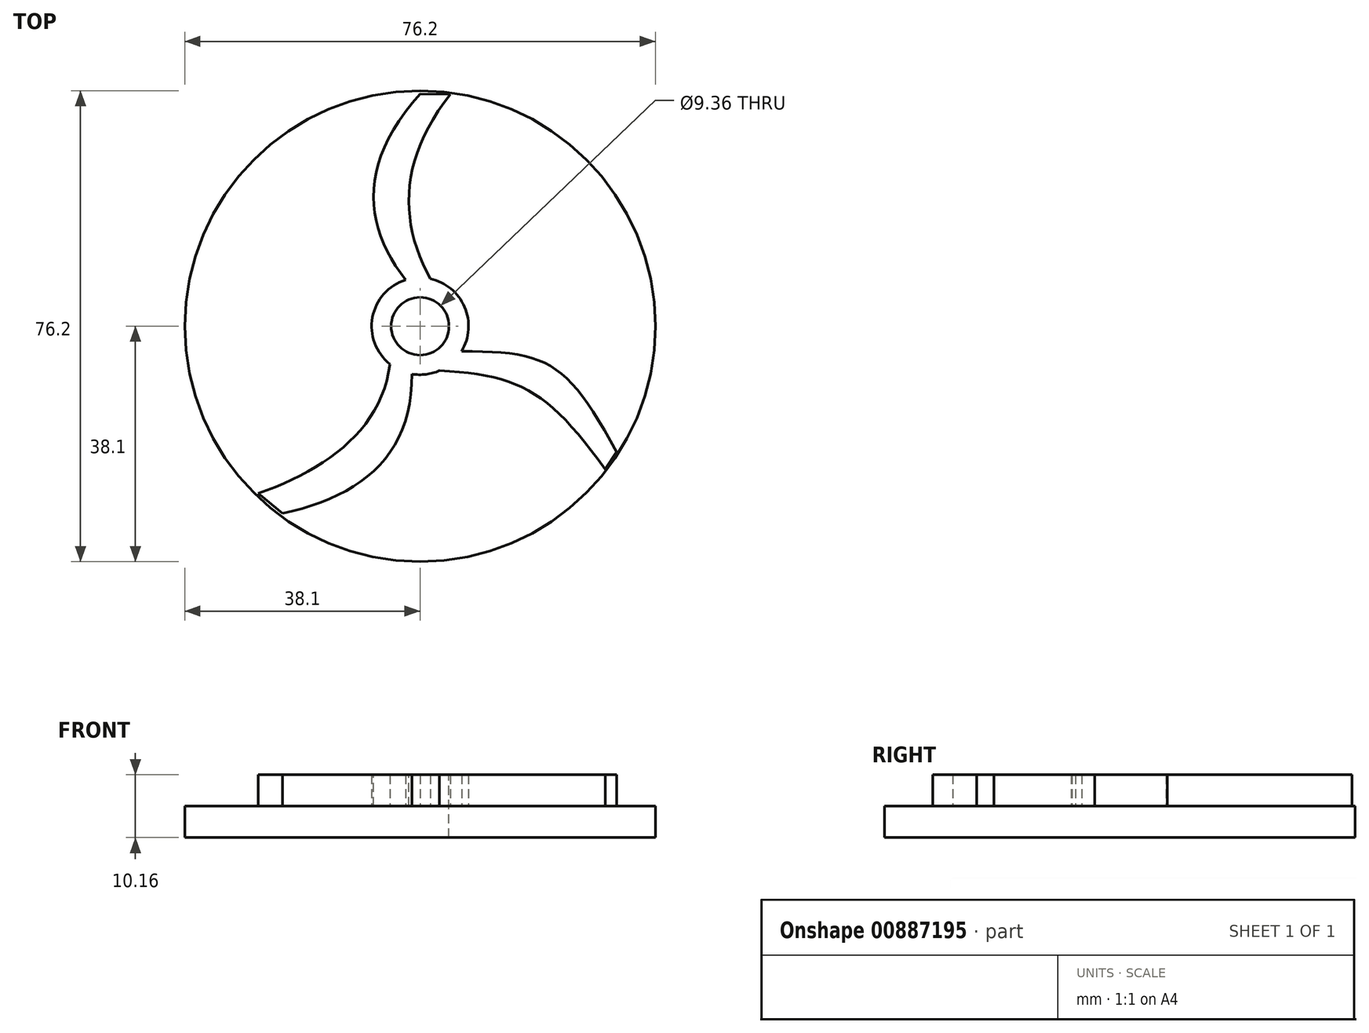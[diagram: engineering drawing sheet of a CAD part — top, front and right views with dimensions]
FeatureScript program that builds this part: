
annotation { "Feature Type Name" : "Feature", "Feature Type Description" : "" }
export const myFeature = defineFeature(function(context is Context, id is Id, definition is map)
    precondition{}
    {
        {
            var Q0;
            Q0=qCreatedBy(makeId("Top.planeOp"),FACE);
            var sketch = newSketch(context, id + "F0", { "sketchPlane" : qUnion([Q0])});
            skCircle(sketch, "E0", {"center": v(0, 0) * mm, "radius": 38.1 * mm});
            skSolve(sketch);
        }
        {
            var Q0;
            Q0=makeQuery(id+"F0.imprint","IMPRINT",FACE,{"disambiguationData":[TD([[makeQuery(id+"F0.imprint","IMPRINT",EDGE,{"derivedFrom":sQuery(id+"F0.wireOp",EDGE,"E0")}),1.0]])]});
            extrude(context, id + "F1", {"entities" : qUnion([Q0]), "depth" : -5.08 * mm, "offsetDistance" : 25.4 * mm});
        }
        {
            var Q0;
            Q0=qCreatedBy(makeId("Top.planeOp"),FACE);
            var sketch = newSketch(context, id + "F2", { "sketchPlane" : qUnion([Q0])});
            skCircle(sketch, "E1", {"center": v(0, 0) * mm, "radius": 7.85 * mm});
            skFitSpline(sketch, "E2", {"points": [v(-2.34, 7.5) * mm, v(0, 37.6) * mm], "startDerivative": vector(-20.28, 26.18) * mm, "endDerivative": vector(30.61, 34.1) * mm});
            skFitSpline(sketch, "E3", {"points": [v(4.92, 37.56) * mm, v(1.64, 7.67) * mm], "startDerivative": vector(-24.96, -31.27) * mm, "endDerivative": vector(15.19, -27.68) * mm});
            skLineSegment(sketch, "E4", {"start": v(0, 37.6) * mm, "end": v(4.92, 37.56) * mm});
            skFitSpline(sketch, "E5", {"points": [v(6.71, -4.06) * mm, v(31.8, -20.36) * mm], "startDerivative": vector(42, 0.07) * mm, "endDerivative": vector(23.72, -43.88) * mm});
            skFitSpline(sketch, "E6", {"points": [v(3.12, -7.2) * mm, v(30, -23.17) * mm], "startDerivative": vector(39.16, -1.84) * mm, "endDerivative": vector(27.29, -37.65) * mm});
            skFitSpline(sketch, "E7", {"points": [v(-4.89, -6.14) * mm, v(-26.23, -27.08) * mm], "startDerivative": vector(-3.93, -31.9) * mm, "endDerivative": vector(-32.7, -11.6) * mm});
            skFitSpline(sketch, "E8", {"points": [v(-1.32, -7.74) * mm, v(-22.3, -30.28) * mm], "startDerivative": vector(0.17, -39.46) * mm, "endDerivative": vector(-38.14, -7.93) * mm});
            skLineSegment(sketch, "E9", {"start": v(-26.23, -27.08) * mm, "end": v(-22.3, -30.28) * mm});
            skLineSegment(sketch, "E10", {"start": v(31.8, -20.36) * mm, "end": v(30, -23.17) * mm});
            skSolve(sketch);
        }
        {
            var Q0;
            Q0 = qSketchRegion(id + "F2", true);
            extrude(context, id + "F3", {"entities" : qUnion([Q0]), "operationType" : NewBodyOperationType.ADD, "depth" : 5.08 * mm, "offsetDistance" : 25.4 * mm});
        }
        {
            var Q0;
            Q0=makeQuery(id+"F3.opExtrude","CAP_FACE",FACE,{"disambiguationData":[OSD([sQuery(id+"F2.wireOp",EDGE,"E1"),sQuery(id+"F2.wireOp",EDGE,"E2"),sQuery(id+"F2.wireOp",EDGE,"E3"),sQuery(id+"F2.wireOp",EDGE,"E4"),sQuery(id+"F2.wireOp",EDGE,"E5"),sQuery(id+"F2.wireOp",EDGE,"E6"),sQuery(id+"F2.wireOp",EDGE,"E7"),sQuery(id+"F2.wireOp",EDGE,"E8"),sQuery(id+"F2.wireOp",EDGE,"E9"),sQuery(id+"F2.wireOp",EDGE,"E10")])],"isStart":false});
            var sketch = newSketch(context, id + "F4", { "sketchPlane" : qUnion([Q0])});
            skCircle(sketch, "E11", {"center": v(0, 0) * mm, "radius": 4.68 * mm});
            skSolve(sketch);
        }
        {
            var Q0;
            Q0 = qSketchRegion(id + "F4", true);
            extrude(context, id + "F5", {"entities" : qUnion([Q0]), "operationType" : NewBodyOperationType.REMOVE, "oppositeDirection" : true, "depth" : 25.4 * mm, "offsetDistance" : 25.4 * mm});
        }
    });
